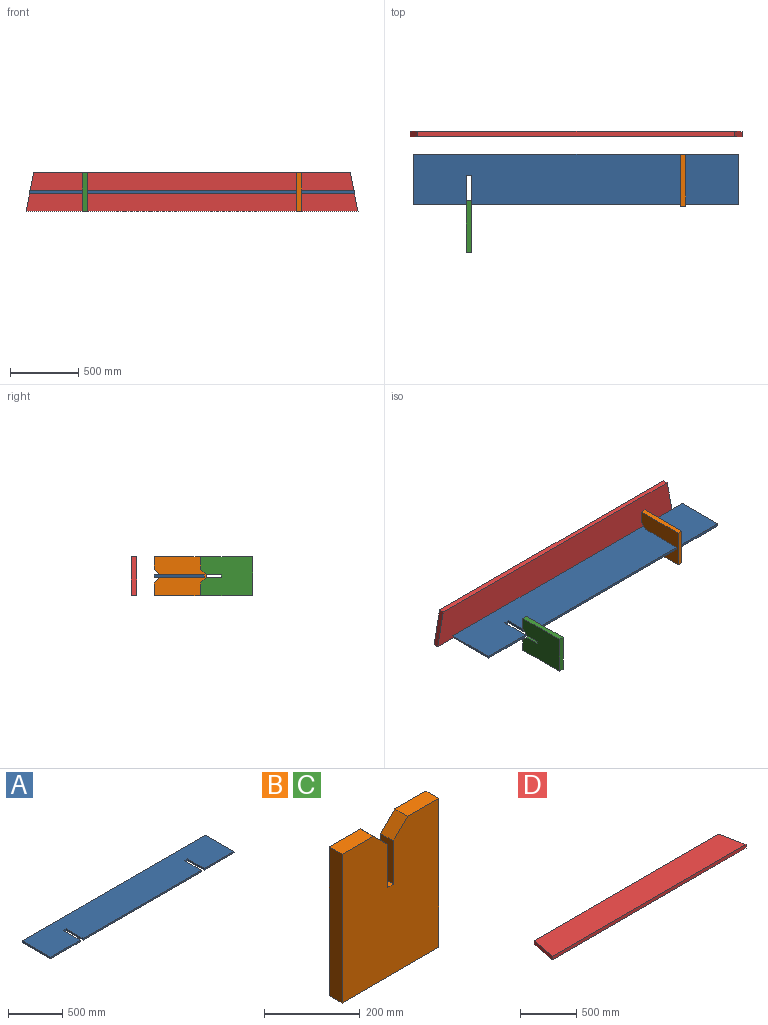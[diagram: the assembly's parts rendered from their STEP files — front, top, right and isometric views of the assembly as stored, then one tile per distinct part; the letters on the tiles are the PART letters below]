
ASSEMBLY  parts=4 mates=3
PART A: 14 faces, bbox 2385x368.3x17.5 mm
  f0: plane 1535.15x17.48mm, normal (0,-1,0), area 26827mm2, adj f2,f3,f8,f13
  f1: plane 386.84x17.48mm, normal (0,-1,0), area 6729.8mm2, adj f2,f3,f5,f10
  f2: plane 2385.03x368.3mm, normal (0,0,-1), area 861955.3mm2, adj f0,f1,f4,f5,f6,f7,f8,f9
  f3: plane 2378.08x368.3mm, normal (0,0,1), area 859394.8mm2, adj f0,f1,f4,f5,f6,f7,f8,f9
  f4: plane 368.3x17.48mm, normal (-0.98,0,0.2), area 6562.2mm2, adj f2,f3,f6,f7
  f5: plane 368.3x17.48mm, normal (0.98,0,0.2), area 6562.2mm2, adj f1,f2,f3,f7
  f6: plane 386.84x17.48mm, normal (0,-1,0), area 6729.8mm2, adj f2,f3,f4,f11
  f7: plane 2385.03x17.48mm, normal (0,1,0), area 41618.1mm2, adj f2,f3,f4,f5
  f8: plane 215.9x17.48mm, normal (1,0,0), area 3772.9mm2, adj f0,f2,f3,f9
  f9: plane 38.1x17.48mm, normal (0,-1,0), area 665.8mm2, adj f2,f3,f8,f10
  f10: plane 215.9x17.48mm, normal (-1,0,0), area 3772.9mm2, adj f1,f2,f3,f9
  f11: plane 215.9x17.48mm, normal (1,0,0), area 3772.9mm2, adj f2,f3,f6,f12
  f12: plane 38.1x17.48mm, normal (0,-1,0), area 665.8mm2, adj f2,f3,f11,f13
  f13: plane 215.9x17.48mm, normal (-1,0,0), area 3772.9mm2, adj f0,f2,f3,f12
PART B: 12 faces, bbox 285.8x38.1x381 mm
  f0: plane 38.1x17.48mm, normal (0,0,1), area 665.8mm2, adj f1,f9,f10,f11
  f1: plane 110.34x38.1mm, normal (1,0,0), area 4203.9mm2, adj f0,f2,f10,f11
  f2: plane 42.06x42.06mm, normal (0.71,0,0.71), area 2266.4mm2, adj f1,f3,f10,f11
  f3: plane 92.08x38.1mm, normal (0,0,1), area 3508.1mm2, adj f2,f4,f10,f11
  f4: plane 381x38.1mm, normal (-1,0,0), area 14516.1mm2, adj f3,f5,f10,f11
  f5: plane 285.75x38.1mm, normal (0,0,-1), area 10887.1mm2, adj f4,f6,f10,f11
  f6: plane 381x38.1mm, normal (1,0,0), area 14516.1mm2, adj f5,f7,f10,f11
  f7: plane 92.08x38.1mm, normal (0,0,1), area 3508.1mm2, adj f6,f8,f10,f11
  f8: plane 42.06x42.06mm, normal (-0.71,0,0.71), area 2266.4mm2, adj f7,f9,f10,f11
  f9: plane 110.34x38.1mm, normal (-1,0,0), area 4203.9mm2, adj f0,f8,f10,f11
  f10: plane 381x285.75mm, normal (0,-1,0), area 104438.3mm2, adj f0,f1,f2,f3,f4,f5,f6,f7
  f11: plane 381x285.75mm, normal (0,1,0), area 104438.3mm2, adj f0,f1,f2,f3,f4,f5,f6,f7
PART C: same geometry as B
PART D: 6 faces, bbox 2438.4x285.8x38.1 mm
  f0: plane 2324.72x38.1mm, normal (0,1,0), area 88571.9mm2, adj f1,f3,f4,f5
  f1: plane 285.75x56.84mm, normal (-0.98,0.2,0), area 11100.4mm2, adj f0,f2,f4,f5
  f2: plane 2438.4x38.1mm, normal (0,-1,0), area 92903mm2, adj f1,f3,f4,f5
  f3: plane 285.75x56.84mm, normal (0.98,0.2,0), area 11100.4mm2, adj f0,f2,f4,f5
  f4: plane 2438.4x285.75mm, normal (0,0,-1), area 680531mm2, adj f0,f1,f2,f3
  f5: plane 2438.4x285.75mm, normal (0,0,1), area 680531mm2, adj f0,f1,f2,f3
PLACE A rot(axis=(0,1,0),180deg) t=(1030.95,277.96,-161.29)mm
PLACE B rot(axis=(-0.58,-0.58,-0.58),120deg) t=(1836.63,-103.04,-170.02)mm
PLACE C rot(axis=(-0.58,-0.58,-0.58),120deg) t=(263.38,-443.25,-170.02)mm
PLACE D rot(axis=(0,-0.71,-0.71),180deg) t=(1030.95,445.71,-168.88)mm
MATE slider A.f7 <-> D.f4  axis (0,1,0) through (1030.95,277.96,-170.02)mm
MATE slider C.f0 <-> A.f9  axis (0,1,0) through (244.33,-214.65,-170.02)mm
MATE slider B.f0 <-> A.f12  axis (0,1,0) through (1817.58,125.56,-170.02)mm
